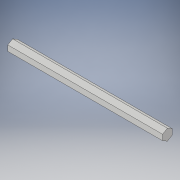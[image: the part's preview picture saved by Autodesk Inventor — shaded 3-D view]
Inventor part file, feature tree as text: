
AUTODESK INVENTOR PART (.ipt)
format: ipt  version: 2018 (Build 220112000, 112)  size: 95,232 bytes
history: native  units: in
note: dims shown in document units (in); Inventor stores cm internally (conversion verified against a paired STEP export)
features: extrude x1, sketch x1
ambient origin geometry x8: Origin, YZ Plane, XZ Plane, XY Plane, X Axis, Y Axis, Z Axis, Center Point
bodies: Solid1 (feature_tree)
feature tree (2):
  extrude  "Extrusion1"  Depth=6.0in TaperAngle=0.0deg
  sketch  "Sketch1"  dims[d0=0.1875in d1=6.0in d2=0.0in]
